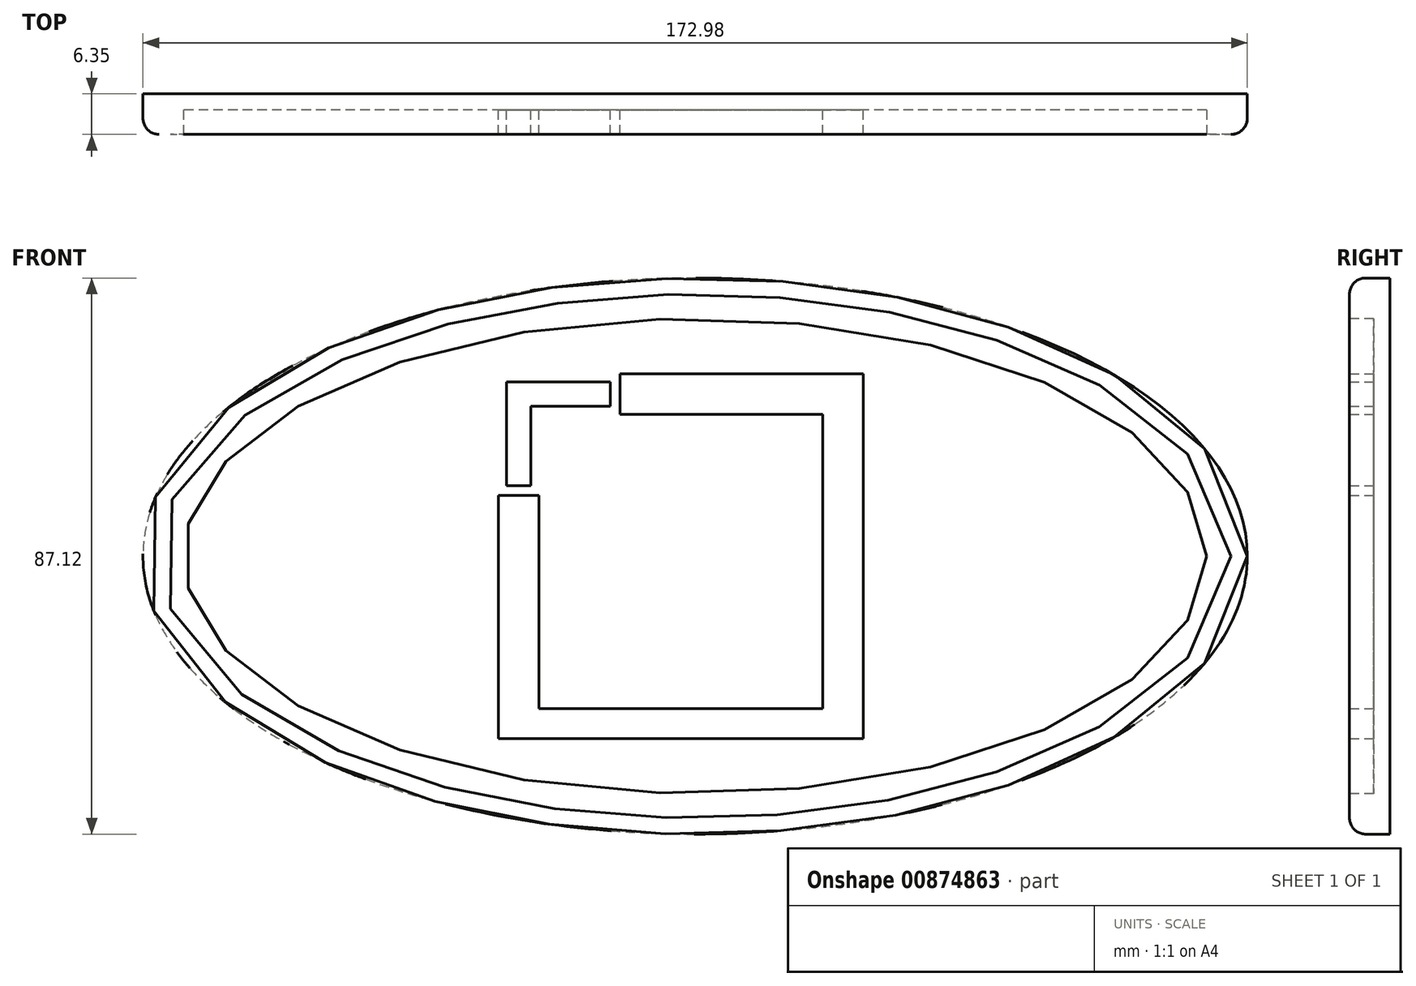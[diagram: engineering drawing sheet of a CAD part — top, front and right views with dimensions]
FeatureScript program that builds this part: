
annotation { "Feature Type Name" : "Feature", "Feature Type Description" : "" }
export const myFeature = defineFeature(function(context is Context, id is Id, definition is map)
    precondition{}
    {
        {
            var Q0;
            Q0=qCreatedBy(makeId("Front.planeOp"),FACE);
            var sketch = newSketch(context, id + "F0", { "sketchPlane" : qUnion([Q0])});
            skEllipse(sketch, "E0", {"center": v(0, 0) * mm, "majorRadius": 86.49 * mm, "minorRadius": 43.56 * mm, "majorAxis": v(1, 0)});
            skSolve(sketch);
        }
        {
            var Q0;
            Q0 = qSketchRegion(id + "F0", true);
            extrude(context, id + "F1", {"entities" : qUnion([Q0]), "depth" : 6.35 * mm, "offsetDistance" : 25.4 * mm});
        }
        {
            var Q0;
            Q0=makeQuery(id+"F1.opExtrude","CAP_FACE",FACE,{"disambiguationData":[OSD([sQuery(id+"F0.wireOp",EDGE,"E0")])],"isStart":false});
            var sketch = newSketch(context, id + "F2", { "sketchPlane" : qUnion([Q0])});
            skEllipse(sketch, "E1", {"center": v(0, 0) * mm, "majorRadius": 80.14 * mm, "minorRadius": 37.21 * mm, "majorAxis": v(1, 0)});
            skSolve(sketch);
        }
        {
            var Q0;
            Q0 = qSketchRegion(id + "F2", true);
            extrude(context, id + "F3", {"entities" : qUnion([Q0]), "operationType" : NewBodyOperationType.REMOVE, "oppositeDirection" : true, "depth" : 3.8 * mm, "offsetDistance" : 25.4 * mm});
        }
        {
            var Q0;
            Q0=makeQuery(id+"F3.boolean.opBoolean","COPY",FACE,{"derivedFrom":makeQuery(id+"F3.opExtrude","CAP_FACE",FACE,{"disambiguationData":[OSD([sQuery(id+"F2.wireOp",EDGE,"E1")])],"isStart":false})});
            var sketch = newSketch(context, id + "F4", { "sketchPlane" : qUnion([Q0])});
            skLineSegment(sketch, "E2", {"start": v(-30.8, 9.48) * mm, "end": v(-30.8, -28.62) * mm});
            skLineSegment(sketch, "E3", {"start": v(-30.8, -28.62) * mm, "end": v(26.34, -28.62) * mm});
            skLineSegment(sketch, "E4", {"start": v(26.34, -28.62) * mm, "end": v(26.34, 28.53) * mm});
            skLineSegment(sketch, "E5", {"start": v(26.34, 28.53) * mm, "end": v(-11.76, 28.53) * mm});
            skLineSegment(sketch, "E6", {"start": v(-11.76, 28.53) * mm, "end": v(-11.76, 22.18) * mm});
            skLineSegment(sketch, "E7", {"start": v(-11.76, 22.18) * mm, "end": v(20, 22.18) * mm});
            skLineSegment(sketch, "E8", {"start": v(20, 22.18) * mm, "end": v(20, -23.88) * mm});
            skLineSegment(sketch, "E9", {"start": v(20, -23.88) * mm, "end": v(-24.46, -23.88) * mm});
            skLineSegment(sketch, "E10", {"start": v(-24.46, -23.88) * mm, "end": v(-24.46, 9.48) * mm});
            skLineSegment(sketch, "E11", {"start": v(-24.46, 9.48) * mm, "end": v(-30.8, 9.48) * mm});
            skLineSegment(sketch, "E12", {"start": v(-29.54, 11) * mm, "end": v(-25.73, 11) * mm});
            skLineSegment(sketch, "E13", {"start": v(-25.73, 11) * mm, "end": v(-25.73, 23.45) * mm});
            skLineSegment(sketch, "E14", {"start": v(-25.73, 23.45) * mm, "end": v(-13.28, 23.45) * mm});
            skLineSegment(sketch, "E15", {"start": v(-13.28, 23.45) * mm, "end": v(-13.28, 27.26) * mm});
            skLineSegment(sketch, "E16", {"start": v(-13.28, 27.26) * mm, "end": v(-29.54, 27.26) * mm});
            skLineSegment(sketch, "E17", {"start": v(-29.54, 27.26) * mm, "end": v(-29.54, 11) * mm});
            skSolve(sketch);
        }
        {
            var Q0;
            Q0 = qSketchRegion(id + "F4", true);
            extrude(context, id + "F5", {"entities" : qUnion([Q0]), "operationType" : NewBodyOperationType.ADD, "depth" : 3.8 * mm, "offsetDistance" : 25.4 * mm});
        }
        {
            var Q0;
            Q0=makeQuery(id+"F1.opExtrude","CAP_EDGE",EDGE,{"disambiguationData":[OSD([sQuery(id+"F0.wireOp",EDGE,"E0")])],"isStart":false});
            fillet(context, id + "F6", {"entities" : qUnion([Q0]), "radius" : 2.54 * mm, "tangentPropagation" : true, "allowEdgeOverflow" : false});
        }
    });
